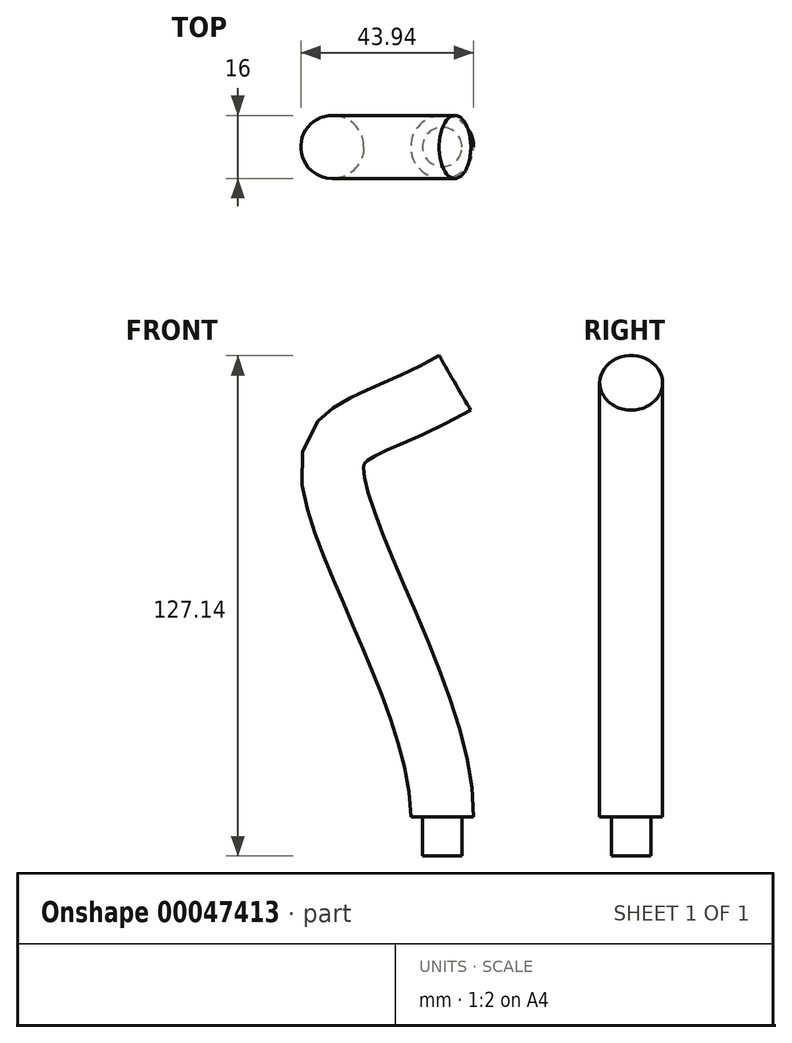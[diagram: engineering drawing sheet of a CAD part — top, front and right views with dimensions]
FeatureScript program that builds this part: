
annotation { "Feature Type Name" : "Feature", "Feature Type Description" : "" }
export const myFeature = defineFeature(function(context is Context, id is Id, definition is map)
    precondition{}
    {
        {
            var Q0;
            Q0=qCreatedBy(makeId("Front.planeOp"),FACE);
            var sketch = newSketch(context, id + "F0", { "sketchPlane" : qUnion([Q0])});
            skFitSpline(sketch, "E0", {"points": [v(0, 0) * mm, v(-27.93, 89.05) * mm, v(3.23, 110.23) * mm], "startDerivative": vector(0, 143.07) * mm, "endDerivative": vector(142.27, 82.79) * mm});
            skSolve(sketch);
        }
        {
            var Q0;
            Q0=qCreatedBy(makeId("Top.planeOp"),FACE);
            var sketch = newSketch(context, id + "F1", { "sketchPlane" : qUnion([Q0])});
            skCircle(sketch, "E1", {"center": v(0, 0) * mm, "radius": 8 * mm});
            skCircle(sketch, "E2", {"center": v(0, 0) * mm, "radius": 5 * mm});
            skSolve(sketch);
        }
        {
            var Q0;
            Q0=makeQuery(id+"F1.imprint","IMPRINT",FACE,{"disambiguationData":[TD([[makeQuery(id+"F1.imprint","IMPRINT",EDGE,{"derivedFrom":sQuery(id+"F1.wireOp",EDGE,"E2")}),1.0]])]});
            extrude(context, id + "F2", {"entities" : qUnion([Q0]), "oppositeDirection" : true, "depth" : 10 * mm});
        }
        {
            var Q0;
            Q0=makeQuery(id+"F1.imprint","IMPRINT",FACE,{"disambiguationData":[TD([[makeQuery(id+"F1.imprint","IMPRINT",EDGE,{"derivedFrom":sQuery(id+"F1.wireOp",EDGE,"E1")}),1.0]])]});
            var Q1;
            Q1=makeQuery(id+"F1.imprint","IMPRINT",FACE,{"disambiguationData":[TD([[makeQuery(id+"F1.imprint","IMPRINT",EDGE,{"derivedFrom":sQuery(id+"F1.wireOp",EDGE,"E2")}),1.0]])]});
            var Q2;
            Q2=sQuery(id+"F0.wireOp",EDGE,"E0");
            sweep(context, id + "F3", {"operationType" : NewBodyOperationType.ADD, "profiles" : qUnion([Q0, Q1]), "path" : qUnion([Q2])});
        }
    });
